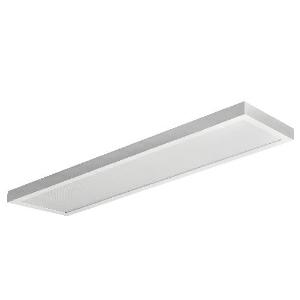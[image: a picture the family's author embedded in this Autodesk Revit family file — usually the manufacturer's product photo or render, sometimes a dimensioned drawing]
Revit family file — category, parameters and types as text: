
# Revit family: ledpanels-sf-p_l15-50w-830_840_542003156200_1f7f
name_source: partatom
category: Lighting Fixtures
units: mm (PartAtom-declared; Revit-internal decimal feet)

## family parameters
Cut with Voids When Loaded = No
Host = Face
Light Source = No
Part Type = Normal
Room Calculation Point = No
Round Connector Dimension = Use Diameter
Shared = No

## types (1)
- LEDPanelS-Sf-P L15-50W-830/840 (1 x LED, 6250 lm, 4000)
    Apparent Load = 50 VA
    Approval mark = CE, ENEC
    CIE Flux Codes = 60 87 97 100 100
    Color Rendering = 80
    Color Temperature = 4000
    Control Gear = Electronic ballast
    Default Elevation = 1800 mm
    Description = Panel Performer Surface Mounted 1574x370mm-50W-6250lm-3/4000K
    Frequency = 60 Hz
    Height = 55 mm
    Lamp = 1 x LED
    Lamp Light Flux = 6250 lm
    Lamp count = 1
    Length = 1574 mm
    Luminous efficacy = 125 lm/W
    Manufacturer = OPPLE
    ModVariant = No
    Model = 542003156200
    Mounting Place = Ceiling
    Mounting Type = Surface mounted
    Number of Poles = 1
    OnlyDefault = Yes
    Power Factor = 1
    Product Name = LEDPanelS-Sf-P L15-50W-830/840
    Product group = Ceiling mounted luminaire
    ProductGroupID = 3
    Protection Class = Protection class II
    Protection Degree = IP 20
    RLX_Detail_Level = 1
    RLX_Emergency_Light_Flux = 0 lm
    RLX_Emergency_Type = 0
    RLX_Emergency_Type_DB = No
    RlxData = <blob elided: 100357 chars, md5=302ef01a>
    Socket = socket
    Standby Power = 0 W
    System Light Flux = 6250 lm
    System Power = 50 W
    Type Comments = Product without accessories
    Type Image = web_surface_pl.jpg
    URL = http://relux.com
    VarID = ---
    Voltage = 230 V
    Voltage Range = 220-240 V
    Weight = 0.00 kg
    Width = 370 mm

## geometry (parser evidence)
native form markers: Blend x4, Sweep x11
no freeform markers — native parametric forms only
